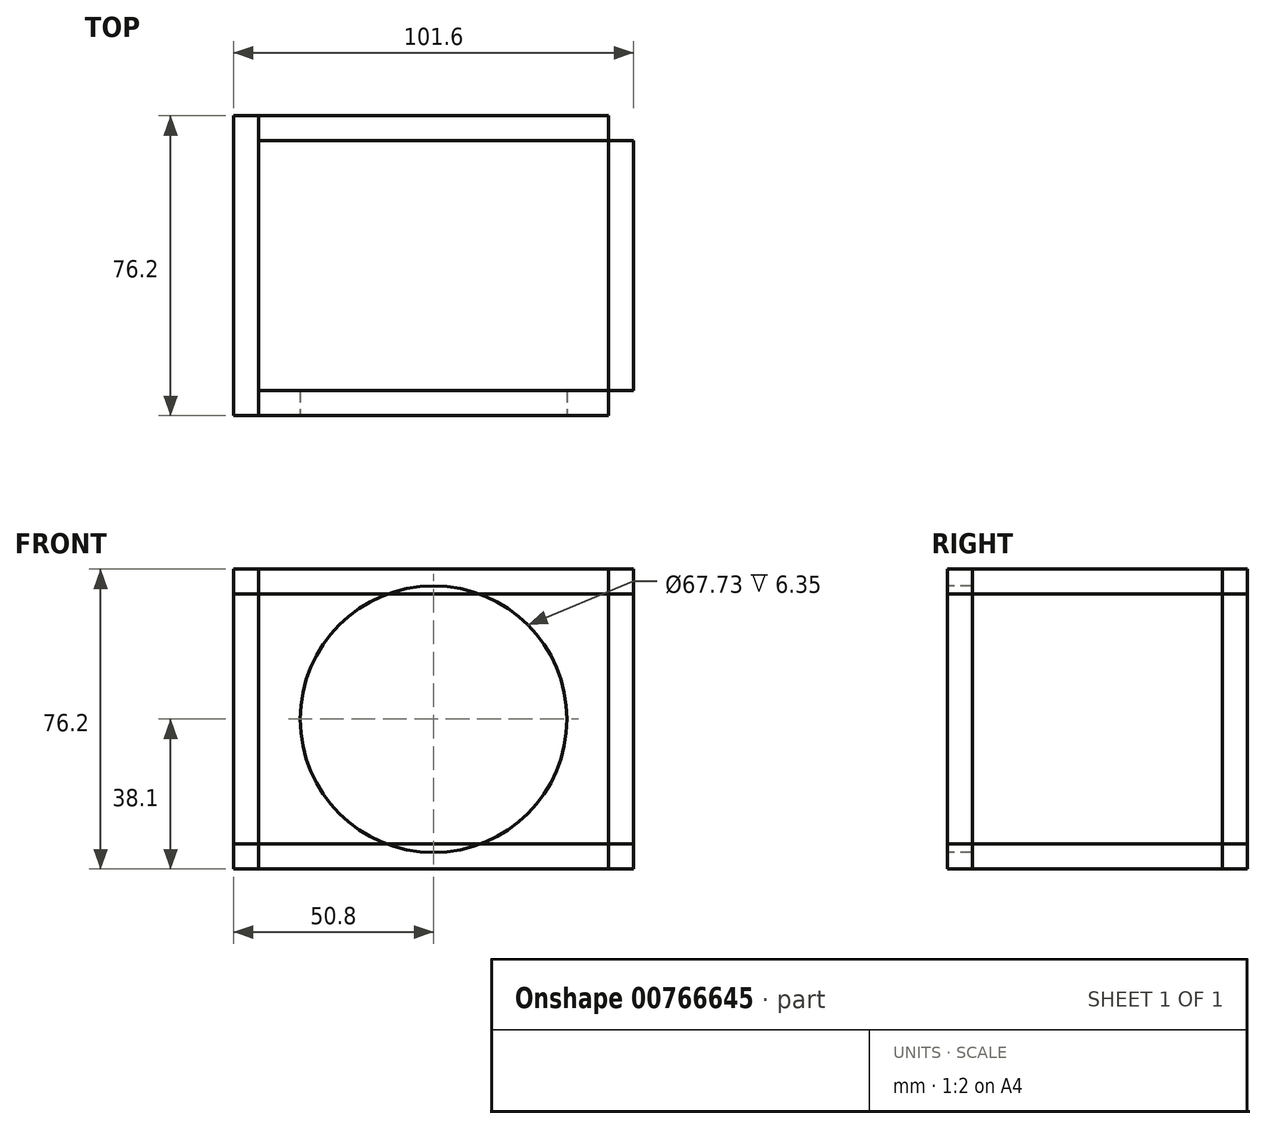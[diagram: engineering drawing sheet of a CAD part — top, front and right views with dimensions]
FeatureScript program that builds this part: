
annotation { "Feature Type Name" : "Feature", "Feature Type Description" : "" }
export const myFeature = defineFeature(function(context is Context, id is Id, definition is map)
    precondition{}
    {
        {
            assignVariable(context, id + "F0", {"name" : "LZ", "anyValue" : 76.2 * mm});
        }
        {
            assignVariable(context, id + "F1", {"name" : "Wall", "anyValue" : 6.35 * mm});
        }
        {
            var Q0;
            Q0=qCreatedBy(makeId("Top.planeOp"),FACE);
            var sketch = newSketch(context, id + "F2", { "sketchPlane" : qUnion([Q0])});
            skLineSegment(sketch, "E0.bottom", {"start": v(0, 76.2) * mm, "end": v(6.35, 76.2) * mm});
            skLineSegment(sketch, "E0.top", {"start": v(0, 0) * mm, "end": v(6.35, 0) * mm});
            skLineSegment(sketch, "E0.left", {"start": v(0, 76.2) * mm, "end": v(0, 0) * mm});
            skLineSegment(sketch, "E0.right", {"start": v(6.35, 76.2) * mm, "end": v(6.35, 0) * mm});
            skLineSegment(sketch, "E1.bottom", {"start": v(0, 0) * mm, "end": v(101.6, 0) * mm});
            skLineSegment(sketch, "E1.top", {"start": v(0, 6.35) * mm, "end": v(101.6, 6.35) * mm});
            skLineSegment(sketch, "E1.left", {"start": v(0, 0) * mm, "end": v(0, 6.35) * mm});
            skLineSegment(sketch, "E1.right", {"start": v(101.6, 0) * mm, "end": v(101.6, 6.35) * mm});
            skLineSegment(sketch, "E2.bottom", {"start": v(0, 76.2) * mm, "end": v(101.6, 76.2) * mm});
            skLineSegment(sketch, "E2.top", {"start": v(0, 69.85) * mm, "end": v(101.6, 69.85) * mm});
            skLineSegment(sketch, "E2.left", {"start": v(0, 76.2) * mm, "end": v(0, 69.85) * mm});
            skLineSegment(sketch, "E2.right", {"start": v(101.6, 76.2) * mm, "end": v(101.6, 69.85) * mm});
            skLineSegment(sketch, "E3.bottom", {"start": v(95.25, 76.2) * mm, "end": v(101.6, 76.2) * mm});
            skLineSegment(sketch, "E3.top", {"start": v(95.25, 0) * mm, "end": v(101.6, 0) * mm});
            skLineSegment(sketch, "E3.left", {"start": v(95.25, 76.2) * mm, "end": v(95.25, 0) * mm});
            skLineSegment(sketch, "E3.right", {"start": v(101.6, 76.2) * mm, "end": v(101.6, 0) * mm});
            skSolve(sketch);
        }
        {
            var Q0;
            {var subQ5=sQuery(id+"F2.wireOp",EDGE,"E3.top");Q0=makeQuery(id+"F2.imprint","IMPRINT",FACE,{"disambiguationData":[TD([[makeQuery(id+"F2.imprint","IMPRINT",EDGE,{"derivedFrom":subQ5}),1.0]])]});}
            var Q1;
            {var subQ0=sQuery(id+"F2.wireOp",EDGE,"E1.bottom");var subQ1=sQuery(id+"F2.wireOp",EDGE,"E0.right");var subQ2=makeQuery(id+"F2.imprint","INTERSECT",VERTEX,{"derivedFrom":[subQ1,subQ0]});Q1=makeQuery(id+"F2.imprint","IMPRINT",FACE,{"disambiguationData":[TD([[makeQuery(id+"F2.imprint","IMPRINT",EDGE,{"disambiguationData":[TD([[subQ2,1.0]])],"derivedFrom":subQ1}),1.0]])]});}
            var Q2;
            {var subQ5=sQuery(id+"F2.wireOp",EDGE,"E1.left");Q2=makeQuery(id+"F2.imprint","IMPRINT",FACE,{"disambiguationData":[TD([[makeQuery(id+"F2.imprint","IMPRINT",EDGE,{"derivedFrom":subQ5}),-1.0]])]});}
            extrude(context, id + "F3", {"entities" : qUnion([Q0, Q1, Q2]), "depth" : getVariable(context, 'LZ'), "offsetDistance" : 25.4 * mm});
        }
        {
            var Q0;
            Q0=makeQuery(id+"F3.opExtrude","SWEPT_FACE",FACE,{"disambiguationData":[OSD([sQuery(id+"F2.wireOp",EDGE,"E1.bottom"),sQuery(id+"F2.wireOp",EDGE,"E3.top")])]});
            var sketch = newSketch(context, id + "F4", { "sketchPlane" : qUnion([Q0])});
            skCircle(sketch, "E4", {"center": v(50.8, 38.1) * mm, "radius": 33.87 * mm});
            skLineSegment(sketch, "E5", {"start": v(50.8, 38.1) * mm, "end": v(50.8, 71.97) * mm, "construction": true});
            skLineSegment(sketch, "E6", {"start": v(50.8, 38.1) * mm, "end": v(84.67, 38.1) * mm, "construction": true});
            skSolve(sketch);
        }
        {
            var Q0;
            Q0=makeQuery(id+"F4.imprint","IMPRINT",FACE,{"disambiguationData":[TD([[makeQuery(id+"F4.imprint","IMPRINT",EDGE,{"derivedFrom":sQuery(id+"F4.wireOp",EDGE,"E4")}),1.0]])]});
            var Q1;
            Q1=makeQuery(id+"F3.opExtrude","SWEPT_FACE",FACE,{"disambiguationData":[OSD([sQuery(id+"F2.wireOp",EDGE,"E1.top")])]});
            extrude(context, id + "F5", {"entities" : qUnion([Q0]), "operationType" : NewBodyOperationType.REMOVE, "endBound" : BoundingType.UP_TO_SURFACE, "oppositeDirection" : true, "depth" : 25.4 * mm, "endBoundEntityFace" : qUnion([Q1]), "offsetDistance" : 25.4 * mm});
        }
        {
            var Q0;
            {var subQ5=sQuery(id+"F2.wireOp",EDGE,"E1.left");Q0=makeQuery(id+"F2.imprint","IMPRINT",FACE,{"disambiguationData":[TD([[makeQuery(id+"F2.imprint","IMPRINT",EDGE,{"derivedFrom":subQ5}),-1.0]])]});}
            var Q1;
            {var subQ0=sQuery(id+"F2.wireOp",EDGE,"E0.left");Q1=makeQuery(id+"F2.imprint","IMPRINT",FACE,{"disambiguationData":[TD([[makeQuery(id+"F2.imprint","IMPRINT",EDGE,{"derivedFrom":subQ0}),1.0]])]});}
            var Q2;
            {var subQ5=sQuery(id+"F2.wireOp",EDGE,"E2.left");Q2=makeQuery(id+"F2.imprint","IMPRINT",FACE,{"disambiguationData":[TD([[makeQuery(id+"F2.imprint","IMPRINT",EDGE,{"derivedFrom":subQ5}),1.0]])]});}
            extrude(context, id + "F6", {"entities" : qUnion([Q0, Q1, Q2]), "depth" : getVariable(context, 'LZ'), "offsetDistance" : 25.4 * mm});
        }
        {
            var Q0;
            {var subQ5=sQuery(id+"F2.wireOp",EDGE,"E2.left");Q0=makeQuery(id+"F2.imprint","IMPRINT",FACE,{"disambiguationData":[TD([[makeQuery(id+"F2.imprint","IMPRINT",EDGE,{"derivedFrom":subQ5}),1.0]])]});}
            var Q1;
            {var subQ0=sQuery(id+"F2.wireOp",EDGE,"E2.bottom");var subQ1=sQuery(id+"F2.wireOp",EDGE,"E0.right");var subQ2=makeQuery(id+"F2.imprint","INTERSECT",VERTEX,{"derivedFrom":[subQ1,subQ0]});Q1=makeQuery(id+"F2.imprint","IMPRINT",FACE,{"disambiguationData":[TD([[makeQuery(id+"F2.imprint","IMPRINT",EDGE,{"disambiguationData":[TD([[subQ2,-1.0]])],"derivedFrom":subQ1}),1.0]])]});}
            var Q2;
            {var subQ5=sQuery(id+"F2.wireOp",EDGE,"E3.bottom");Q2=makeQuery(id+"F2.imprint","IMPRINT",FACE,{"disambiguationData":[TD([[makeQuery(id+"F2.imprint","IMPRINT",EDGE,{"derivedFrom":subQ5}),-1.0]])]});}
            extrude(context, id + "F7", {"entities" : qUnion([Q0, Q1, Q2]), "depth" : getVariable(context, 'LZ'), "offsetDistance" : 25.4 * mm});
        }
        {
            var Q0;
            {var subQ5=sQuery(id+"F2.wireOp",EDGE,"E3.bottom");Q0=makeQuery(id+"F2.imprint","IMPRINT",FACE,{"disambiguationData":[TD([[makeQuery(id+"F2.imprint","IMPRINT",EDGE,{"derivedFrom":subQ5}),-1.0]])]});}
            var Q1;
            {var subQ0=sQuery(id+"F2.wireOp",EDGE,"E3.right");var subQ1=sQuery(id+"F2.wireOp",EDGE,"E1.top");var subQ2=makeQuery(id+"F2.imprint","INTERSECT",VERTEX,{"derivedFrom":[subQ1,subQ0]});Q1=makeQuery(id+"F2.imprint","IMPRINT",FACE,{"disambiguationData":[TD([[makeQuery(id+"F2.imprint","IMPRINT",EDGE,{"disambiguationData":[TD([[subQ2,1.0]])],"derivedFrom":subQ1}),1.0]])]});}
            var Q2;
            {var subQ5=sQuery(id+"F2.wireOp",EDGE,"E3.top");Q2=makeQuery(id+"F2.imprint","IMPRINT",FACE,{"disambiguationData":[TD([[makeQuery(id+"F2.imprint","IMPRINT",EDGE,{"derivedFrom":subQ5}),1.0]])]});}
            extrude(context, id + "F8", {"entities" : qUnion([Q0, Q1, Q2]), "depth" : getVariable(context, 'LZ'), "offsetDistance" : 25.4 * mm});
        }
        {
            var Q0;
            {var subQ5=sQuery(id+"F2.wireOp",EDGE,"E1.left");Q0=makeQuery(id+"F2.imprint","IMPRINT",FACE,{"disambiguationData":[TD([[makeQuery(id+"F2.imprint","IMPRINT",EDGE,{"derivedFrom":subQ5}),-1.0]])]});}
            var Q1;
            {var subQ0=sQuery(id+"F2.wireOp",EDGE,"E0.left");Q1=makeQuery(id+"F2.imprint","IMPRINT",FACE,{"disambiguationData":[TD([[makeQuery(id+"F2.imprint","IMPRINT",EDGE,{"derivedFrom":subQ0}),1.0]])]});}
            var Q2;
            {var subQ5=sQuery(id+"F2.wireOp",EDGE,"E2.left");Q2=makeQuery(id+"F2.imprint","IMPRINT",FACE,{"disambiguationData":[TD([[makeQuery(id+"F2.imprint","IMPRINT",EDGE,{"derivedFrom":subQ5}),1.0]])]});}
            var Q3;
            {var subQ0=sQuery(id+"F2.wireOp",EDGE,"E2.bottom");var subQ1=sQuery(id+"F2.wireOp",EDGE,"E0.right");var subQ2=makeQuery(id+"F2.imprint","INTERSECT",VERTEX,{"derivedFrom":[subQ1,subQ0]});Q3=makeQuery(id+"F2.imprint","IMPRINT",FACE,{"disambiguationData":[TD([[makeQuery(id+"F2.imprint","IMPRINT",EDGE,{"disambiguationData":[TD([[subQ2,-1.0]])],"derivedFrom":subQ1}),1.0]])]});}
            var Q4;
            {var subQ5=sQuery(id+"F2.wireOp",EDGE,"E3.bottom");Q4=makeQuery(id+"F2.imprint","IMPRINT",FACE,{"disambiguationData":[TD([[makeQuery(id+"F2.imprint","IMPRINT",EDGE,{"derivedFrom":subQ5}),-1.0]])]});}
            var Q5;
            {var subQ0=sQuery(id+"F2.wireOp",EDGE,"E3.right");var subQ1=sQuery(id+"F2.wireOp",EDGE,"E1.top");var subQ2=makeQuery(id+"F2.imprint","INTERSECT",VERTEX,{"derivedFrom":[subQ1,subQ0]});Q5=makeQuery(id+"F2.imprint","IMPRINT",FACE,{"disambiguationData":[TD([[makeQuery(id+"F2.imprint","IMPRINT",EDGE,{"disambiguationData":[TD([[subQ2,1.0]])],"derivedFrom":subQ1}),1.0]])]});}
            var Q6;
            {var subQ5=sQuery(id+"F2.wireOp",EDGE,"E3.top");Q6=makeQuery(id+"F2.imprint","IMPRINT",FACE,{"disambiguationData":[TD([[makeQuery(id+"F2.imprint","IMPRINT",EDGE,{"derivedFrom":subQ5}),1.0]])]});}
            var Q7;
            {var subQ0=sQuery(id+"F2.wireOp",EDGE,"E2.top");var subQ1=sQuery(id+"F2.wireOp",EDGE,"E0.right");var subQ2=makeQuery(id+"F2.imprint","INTERSECT",VERTEX,{"derivedFrom":[subQ1,subQ0]});Q7=makeQuery(id+"F2.imprint","IMPRINT",FACE,{"disambiguationData":[TD([[makeQuery(id+"F2.imprint","IMPRINT",EDGE,{"disambiguationData":[TD([[subQ2,-1.0]])],"derivedFrom":subQ1}),1.0]])]});}
            var Q8;
            {var subQ0=sQuery(id+"F2.wireOp",EDGE,"E1.bottom");var subQ1=sQuery(id+"F2.wireOp",EDGE,"E0.right");var subQ2=makeQuery(id+"F2.imprint","INTERSECT",VERTEX,{"derivedFrom":[subQ1,subQ0]});Q8=makeQuery(id+"F2.imprint","IMPRINT",FACE,{"disambiguationData":[TD([[makeQuery(id+"F2.imprint","IMPRINT",EDGE,{"disambiguationData":[TD([[subQ2,1.0]])],"derivedFrom":subQ1}),1.0]])]});}
            extrude(context, id + "F9", {"entities" : qUnion([Q0, Q1, Q2, Q3, Q4, Q5, Q6, Q7, Q8]), "depth" : getVariable(context, 'LZ'), "offsetDistance" : 25.4 * mm, "hasSecondDirection" : true, "secondDirectionOppositeDirection" : false, "secondDirectionDepth" : getVariable(context, 'LZ') - getVariable(context, 'Wall')});
        }
        {
            var Q0;
            {var subQ5=sQuery(id+"F2.wireOp",EDGE,"E1.left");Q0=makeQuery(id+"F2.imprint","IMPRINT",FACE,{"disambiguationData":[TD([[makeQuery(id+"F2.imprint","IMPRINT",EDGE,{"derivedFrom":subQ5}),-1.0]])]});}
            var Q1;
            {var subQ0=sQuery(id+"F2.wireOp",EDGE,"E0.left");Q1=makeQuery(id+"F2.imprint","IMPRINT",FACE,{"disambiguationData":[TD([[makeQuery(id+"F2.imprint","IMPRINT",EDGE,{"derivedFrom":subQ0}),1.0]])]});}
            var Q2;
            {var subQ5=sQuery(id+"F2.wireOp",EDGE,"E2.left");Q2=makeQuery(id+"F2.imprint","IMPRINT",FACE,{"disambiguationData":[TD([[makeQuery(id+"F2.imprint","IMPRINT",EDGE,{"derivedFrom":subQ5}),1.0]])]});}
            var Q3;
            {var subQ0=sQuery(id+"F2.wireOp",EDGE,"E2.bottom");var subQ1=sQuery(id+"F2.wireOp",EDGE,"E0.right");var subQ2=makeQuery(id+"F2.imprint","INTERSECT",VERTEX,{"derivedFrom":[subQ1,subQ0]});Q3=makeQuery(id+"F2.imprint","IMPRINT",FACE,{"disambiguationData":[TD([[makeQuery(id+"F2.imprint","IMPRINT",EDGE,{"disambiguationData":[TD([[subQ2,-1.0]])],"derivedFrom":subQ1}),1.0]])]});}
            var Q4;
            {var subQ5=sQuery(id+"F2.wireOp",EDGE,"E3.bottom");Q4=makeQuery(id+"F2.imprint","IMPRINT",FACE,{"disambiguationData":[TD([[makeQuery(id+"F2.imprint","IMPRINT",EDGE,{"derivedFrom":subQ5}),-1.0]])]});}
            var Q5;
            {var subQ0=sQuery(id+"F2.wireOp",EDGE,"E3.right");var subQ1=sQuery(id+"F2.wireOp",EDGE,"E1.top");var subQ2=makeQuery(id+"F2.imprint","INTERSECT",VERTEX,{"derivedFrom":[subQ1,subQ0]});Q5=makeQuery(id+"F2.imprint","IMPRINT",FACE,{"disambiguationData":[TD([[makeQuery(id+"F2.imprint","IMPRINT",EDGE,{"disambiguationData":[TD([[subQ2,1.0]])],"derivedFrom":subQ1}),1.0]])]});}
            var Q6;
            {var subQ5=sQuery(id+"F2.wireOp",EDGE,"E3.top");Q6=makeQuery(id+"F2.imprint","IMPRINT",FACE,{"disambiguationData":[TD([[makeQuery(id+"F2.imprint","IMPRINT",EDGE,{"derivedFrom":subQ5}),1.0]])]});}
            var Q7;
            {var subQ0=sQuery(id+"F2.wireOp",EDGE,"E1.bottom");var subQ1=sQuery(id+"F2.wireOp",EDGE,"E0.right");var subQ2=makeQuery(id+"F2.imprint","INTERSECT",VERTEX,{"derivedFrom":[subQ1,subQ0]});Q7=makeQuery(id+"F2.imprint","IMPRINT",FACE,{"disambiguationData":[TD([[makeQuery(id+"F2.imprint","IMPRINT",EDGE,{"disambiguationData":[TD([[subQ2,1.0]])],"derivedFrom":subQ1}),1.0]])]});}
            var Q8;
            {var subQ0=sQuery(id+"F2.wireOp",EDGE,"E2.top");var subQ1=sQuery(id+"F2.wireOp",EDGE,"E0.right");var subQ2=makeQuery(id+"F2.imprint","INTERSECT",VERTEX,{"derivedFrom":[subQ1,subQ0]});Q8=makeQuery(id+"F2.imprint","IMPRINT",FACE,{"disambiguationData":[TD([[makeQuery(id+"F2.imprint","IMPRINT",EDGE,{"disambiguationData":[TD([[subQ2,-1.0]])],"derivedFrom":subQ1}),1.0]])]});}
            extrude(context, id + "F10", {"entities" : qUnion([Q0, Q1, Q2, Q3, Q4, Q5, Q6, Q7, Q8]), "depth" : getVariable(context, 'Wall'), "offsetDistance" : 25.4 * mm});
        }
    });
